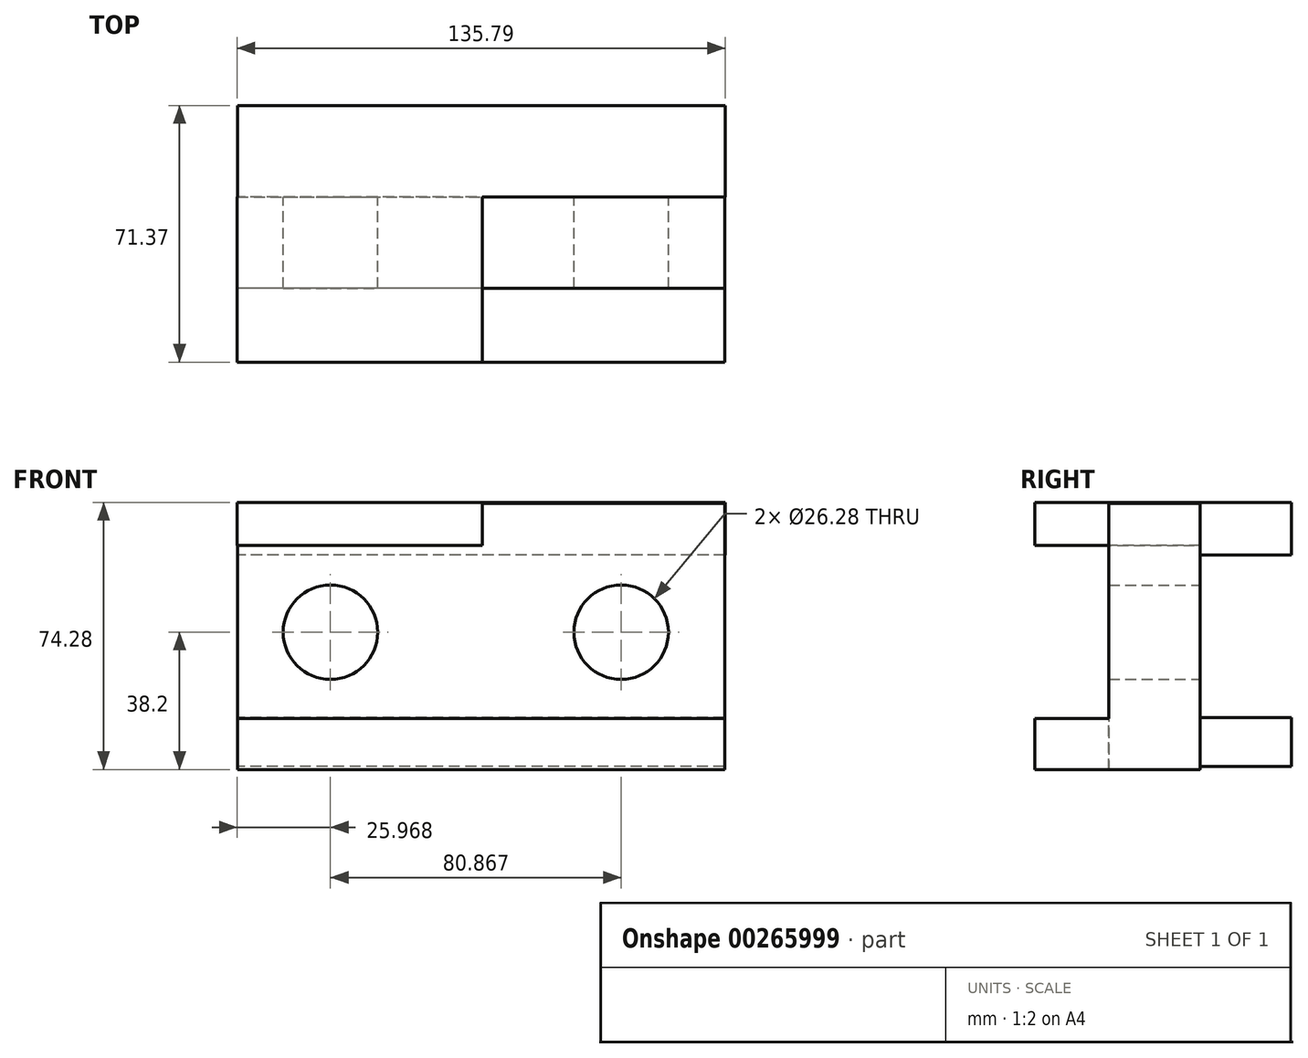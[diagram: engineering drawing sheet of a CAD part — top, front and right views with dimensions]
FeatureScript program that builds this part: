
annotation { "Feature Type Name" : "Feature", "Feature Type Description" : "" }
export const myFeature = defineFeature(function(context is Context, id is Id, definition is map)
    precondition{}
    {
        {
            var Q0;
            Q0=qCreatedBy(makeId("Front.planeOp"),FACE);
            var sketch = newSketch(context, id + "F0", { "sketchPlane" : qUnion([Q0])});
            skLineSegment(sketch, "E0.bottom", {"start": v(-68.07, 35.83) * mm, "end": v(67.48, 35.83) * mm});
            skLineSegment(sketch, "E0.top", {"start": v(-68.07, -38.16) * mm, "end": v(67.48, -38.16) * mm});
            skLineSegment(sketch, "E0.left", {"start": v(-68.07, 35.83) * mm, "end": v(-68.07, -38.16) * mm});
            skLineSegment(sketch, "E0.right", {"start": v(67.48, 35.83) * mm, "end": v(67.48, -38.16) * mm});
            skCircle(sketch, "E1", {"center": v(-42.2, 0) * mm, "radius": 13.14 * mm});
            skCircle(sketch, "E2", {"center": v(38.67, 0) * mm, "radius": 13.14 * mm});
            skSolve(sketch);
        }
        {
            var Q0;
            Q0 = qSketchRegion(id + "F0", true);
            extrude(context, id + "F1", {"entities" : qUnion([Q0]), "depth" : 25.4 * mm});
        }
        {
            var Q0;
            Q0=qCreatedBy(makeId("Front.planeOp"),FACE);
            var sketch = newSketch(context, id + "F2", { "sketchPlane" : qUnion([Q0])});
            skLineSegment(sketch, "E3.bottom", {"start": v(-68.05, -24.04) * mm, "end": v(67.47, -24.04) * mm});
            skLineSegment(sketch, "E3.top", {"start": v(-68.05, -38.2) * mm, "end": v(67.47, -38.2) * mm});
            skLineSegment(sketch, "E3.left", {"start": v(-68.05, -24.04) * mm, "end": v(-68.05, -38.2) * mm});
            skLineSegment(sketch, "E3.right", {"start": v(67.47, -24.04) * mm, "end": v(67.47, -38.2) * mm});
            skLineSegment(sketch, "E4.bottom", {"start": v(-68.17, 36.08) * mm, "end": v(0, 36.08) * mm});
            skLineSegment(sketch, "E4.top", {"start": v(-68.17, 24.12) * mm, "end": v(0, 24.12) * mm});
            skLineSegment(sketch, "E4.left", {"start": v(-68.17, 36.08) * mm, "end": v(-68.17, 24.12) * mm});
            skLineSegment(sketch, "E4.right", {"start": v(0, 36.08) * mm, "end": v(0, 24.12) * mm});
            skSolve(sketch);
        }
        {
            var Q0;
            Q0 = qSketchRegion(id + "F2", true);
            extrude(context, id + "F3", {"entities" : qUnion([Q0]), "operationType" : NewBodyOperationType.ADD, "depth" : 45.97 * mm});
        }
        {
            var Q0;
            Q0=qCreatedBy(makeId("Front.planeOp"),FACE);
            var sketch = newSketch(context, id + "F4", { "sketchPlane" : qUnion([Q0])});
            skLineSegment(sketch, "E5.bottom", {"start": v(67.62, 36.08) * mm, "end": v(-68.04, 36.08) * mm});
            skLineSegment(sketch, "E5.top", {"start": v(67.62, 21.4) * mm, "end": v(-68.04, 21.4) * mm});
            skLineSegment(sketch, "E5.left", {"start": v(67.62, 36.08) * mm, "end": v(67.62, 21.4) * mm});
            skLineSegment(sketch, "E5.right", {"start": v(-68.04, 36.08) * mm, "end": v(-68.04, 21.4) * mm});
            skLineSegment(sketch, "E6.bottom", {"start": v(67.35, -37.33) * mm, "end": v(-68.04, -37.33) * mm});
            skLineSegment(sketch, "E6.top", {"start": v(67.35, -23.74) * mm, "end": v(-68.04, -23.74) * mm});
            skLineSegment(sketch, "E6.left", {"start": v(67.35, -37.33) * mm, "end": v(67.35, -23.74) * mm});
            skLineSegment(sketch, "E6.right", {"start": v(-68.04, -37.33) * mm, "end": v(-68.04, -23.74) * mm});
            skSolve(sketch);
        }
        {
            var Q0;
            Q0 = qSketchRegion(id + "F4", true);
            extrude(context, id + "F5", {"entities" : qUnion([Q0]), "operationType" : NewBodyOperationType.ADD, "oppositeDirection" : true, "depth" : 25.4 * mm});
        }
    });
